# Revit family: 201_PRR-SD-R-_-B-_+NKSD-R
name_source: partatom
category: Air Terminals
units: mm (PartAtom-declared; Revit-internal decimal feet)

## family parameters
Always vertical = Yes
Cut with Voids When Loaded = No
Part Type = Normal
Room Calculation Point = Yes
Round Connector Dimension = Use Diameter
Shared = No
Work Plane-Based = No

## types (3) — shared parameters
CL_Location_5000 = 5000 mm  [stored 16.4042 ft]
D = 160 mm
DZ = 5 mm  [stored 0.0164042 ft]
Description = EXPANSION BOXES TO BE MOUNTED UNDER THE NK-SWA DIFFUSERS
L_ARR = 400 mm  [stored 1.31234 ft]
Manufacturer = Alnor
QmdConnectorList = 201;D
R = 80 mm  [stored 0.262467 ft]
SW1 = Yes
SW10 = Yes
SW2 = No
URL = http://www.ventilation-alnor.co.uk
W_ARR = 400 mm  [stored 1.31234 ft]
XRefLineVPlnId = 7453
YRefLineVPlnId = 7456
magiPartTypeId = 201
magiProductFamilyId = PRR-SD-R-*-B-*+NKSD-R
zero-valued in all types: CLBTZ, H_ARR

## per-type parameters (varying)
| type | A | C1 | DPX | DPZ | DS | XX |
| PRR-SD-R-400-B-125+NKSD-R | 400 mm  [stored 1.31234 ft] | 250 mm  [stored 0.82021 ft] | 195 mm  [stored 0.639764 ft] | 125 mm  [stored 0.410105 ft] | 390 mm  [stored 1.27953 ft] | 39 mm  [stored 0.127953 ft] |
| PRR-SD-R-600-B-200+NKSD-R | 600 mm | 350 mm | 295 mm | 175 mm | 590 mm | 59 mm |
| PRR-SD-R-500-B-160+NKSD-R | 500 mm | 300 mm | 245 mm | 150 mm | 490 mm | 49 mm |

note: column(s) folded — value = type name in every type: MC Product Code, magiProductId

note: [stored X ft] marks values corroborated as IEEE doubles in the binary element streams (Revit-internal decimal feet)

## geometry (parser evidence)
native form markers: Blend x2, Sweep x2
no freeform markers — native parametric forms only
